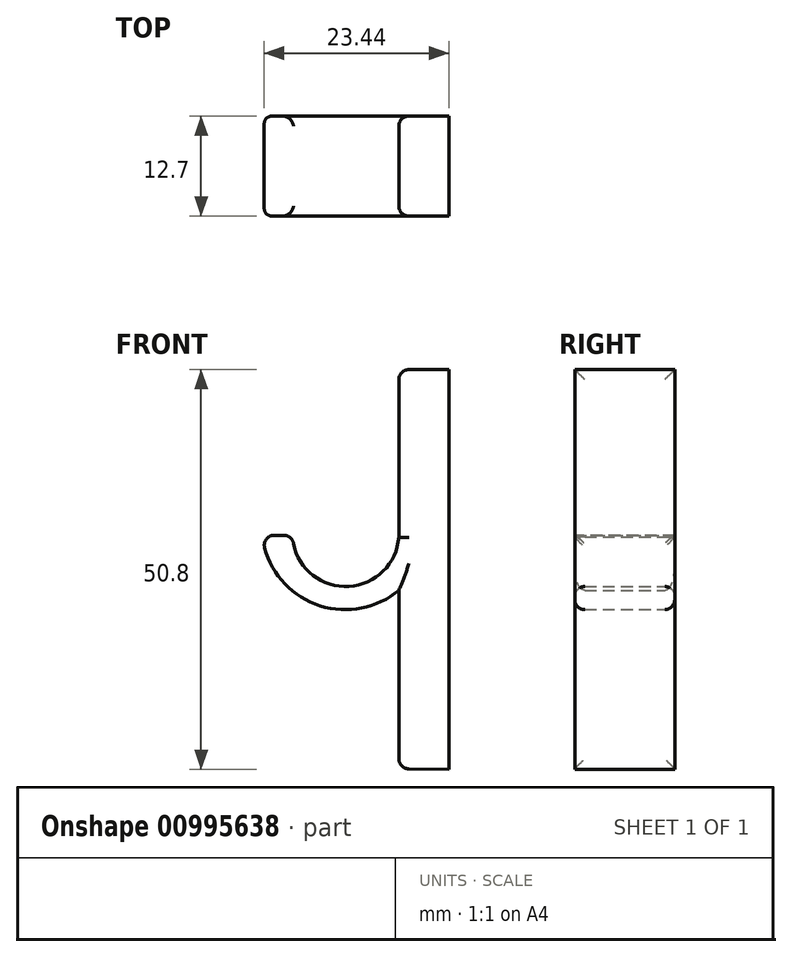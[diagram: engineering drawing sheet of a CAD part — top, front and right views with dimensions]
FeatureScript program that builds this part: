
annotation { "Feature Type Name" : "Feature", "Feature Type Description" : "" }
export const myFeature = defineFeature(function(context is Context, id is Id, definition is map)
    precondition{}
    {
        {
            var Q0;
            Q0=qCreatedBy(makeId("Front.planeOp"),FACE);
            var sketch = newSketch(context, id + "F0", { "sketchPlane" : qUnion([Q0])});
            skLineSegment(sketch, "E0", {"start": v(33.94, 25.03) * mm, "end": v(33.94, -25.77) * mm});
            skLineSegment(sketch, "E1", {"start": v(33.94, 25.03) * mm, "end": v(27.6, 25.03) * mm});
            skLineSegment(sketch, "E2", {"start": v(27.6, 25.03) * mm, "end": v(27.6, -25.67) * mm});
            skLineSegment(sketch, "E3", {"start": v(27.6, -25.67) * mm, "end": v(33.94, -25.77) * mm});
            skArc(sketch, "E4", {"start": v(14.1, 3.98) * mm, "mid": v(20.73, -2.53) * mm, "end": v(27.6, 3.74) * mm});
            skArc(sketch, "E5", {"start": v(10.24, 3.98) * mm, "mid": v(16.83, -4.7) * mm, "end": v(27.6, -3.01) * mm});
            skLineSegment(sketch, "E6", {"start": v(10.24, 3.98) * mm, "end": v(14.1, 3.98) * mm});
            skSolve(sketch);
        }
        {
            var Q0;
            Q0=makeQuery(id+"F0.imprint","IMPRINT",FACE,{"disambiguationData":[TD([[makeQuery(id+"F0.imprint","IMPRINT",EDGE,{"derivedFrom":sQuery(id+"F0.wireOp",EDGE,"E0")}),-1.0]])]});
            var Q1;
            {var subQ0=sQuery(id+"F0.wireOp",EDGE,"E4");Q1=makeQuery(id+"F0.imprint","IMPRINT",FACE,{"disambiguationData":[TD([[makeQuery(id+"F0.imprint","IMPRINT",EDGE,{"derivedFrom":subQ0}),-1.0]])]});}
            extrude(context, id + "F1", {"entities" : qUnion([Q0, Q1]), "depth" : 12.7 * mm, "offsetDistance" : 25.4 * mm});
        }
        {
            var Q0;
            Q0=makeQuery(id+"F1.opExtrude","CAP_EDGE",EDGE,{"disambiguationData":[OSD([sQuery(id+"F0.wireOp",EDGE,"E4")])],"isStart":false});
            var Q1;
            Q1=makeQuery(id+"F1.opExtrude","SWEPT_EDGE",EDGE,{"disambiguationData":[OSD([sQuery(id+"F0.wireOp",EDGE,"E4"),sQuery(id+"F0.wireOp",EDGE,"E6")])]});
            var Q2;
            Q2=makeQuery(id+"F1.opExtrude","CAP_EDGE",EDGE,{"disambiguationData":[OSD([sQuery(id+"F0.wireOp",EDGE,"E4")])],"isStart":true});
            var Q3;
            {var subQ0=sQuery(id+"F0.wireOp",EDGE,"E2");Q3=makeQuery(id+"F1.opExtrude","CAP_EDGE",EDGE,{"disambiguationData":[OSD([subQ0]),TDD([makeQuery(id+"F0.imprint","IMPRINT",EDGE,{"disambiguationData":[TD([[makeQuery(id+"F0.imprint","INTERSECT",VERTEX,{"derivedFrom":[sQuery(id+"F0.wireOp",EDGE,"E1"),subQ0]}),-1.0]])],"derivedFrom":subQ0})])],"isStart":true});}
            var Q4;
            {var subQ0=sQuery(id+"F0.wireOp",EDGE,"E2");Q4=makeQuery(id+"F1.opExtrude","CAP_EDGE",EDGE,{"disambiguationData":[OSD([subQ0]),TDD([makeQuery(id+"F0.imprint","IMPRINT",EDGE,{"disambiguationData":[TD([[makeQuery(id+"F0.imprint","INTERSECT",VERTEX,{"derivedFrom":[sQuery(id+"F0.wireOp",EDGE,"E1"),subQ0]}),-1.0]])],"derivedFrom":subQ0})])],"isStart":false});}
            var Q5;
            Q5=makeQuery(id+"F1.opExtrude","SWEPT_EDGE",EDGE,{"disambiguationData":[OSD([sQuery(id+"F0.wireOp",EDGE,"E1"),sQuery(id+"F0.wireOp",EDGE,"E2")])]});
            var Q6;
            Q6=makeQuery(id+"F1.opExtrude","SWEPT_EDGE",EDGE,{"disambiguationData":[OSD([sQuery(id+"F0.wireOp",EDGE,"E2"),sQuery(id+"F0.wireOp",EDGE,"E3")])]});
            var Q7;
            Q7=makeQuery(id+"F1.opExtrude","CAP_EDGE",EDGE,{"disambiguationData":[OSD([sQuery(id+"F0.wireOp",EDGE,"E5")])],"isStart":true});
            var Q8;
            Q8=makeQuery(id+"F1.opExtrude","CAP_EDGE",EDGE,{"disambiguationData":[OSD([sQuery(id+"F0.wireOp",EDGE,"E5")])],"isStart":false});
            var Q9;
            Q9=makeQuery(id+"F1.opExtrude","SWEPT_EDGE",EDGE,{"disambiguationData":[OSD([sQuery(id+"F0.wireOp",EDGE,"E5"),sQuery(id+"F0.wireOp",EDGE,"E6")])]});
            var Q10;
            {var subQ0=sQuery(id+"F0.wireOp",EDGE,"E2");Q10=makeQuery(id+"F1.opExtrude","CAP_EDGE",EDGE,{"disambiguationData":[OSD([subQ0]),TDD([makeQuery(id+"F0.imprint","IMPRINT",EDGE,{"disambiguationData":[TD([[makeQuery(id+"F0.imprint","INTERSECT",VERTEX,{"derivedFrom":[subQ0,sQuery(id+"F0.wireOp",EDGE,"E3")]}),1.0]])],"derivedFrom":subQ0})])],"isStart":false});}
            var Q11;
            {var subQ0=sQuery(id+"F0.wireOp",EDGE,"E2");Q11=makeQuery(id+"F1.opExtrude","CAP_EDGE",EDGE,{"disambiguationData":[OSD([subQ0]),TDD([makeQuery(id+"F0.imprint","IMPRINT",EDGE,{"disambiguationData":[TD([[makeQuery(id+"F0.imprint","INTERSECT",VERTEX,{"derivedFrom":[subQ0,sQuery(id+"F0.wireOp",EDGE,"E3")]}),1.0]])],"derivedFrom":subQ0})])],"isStart":true});}
            fillet(context, id + "F2", {"entities" : qUnion([Q0, Q1, Q2, Q3, Q4, Q5, Q6, Q7, Q8, Q9, Q10, Q11]), "radius" : 1.27 * mm, "tangentPropagation" : true, "allowEdgeOverflow" : false});
        }
    });
